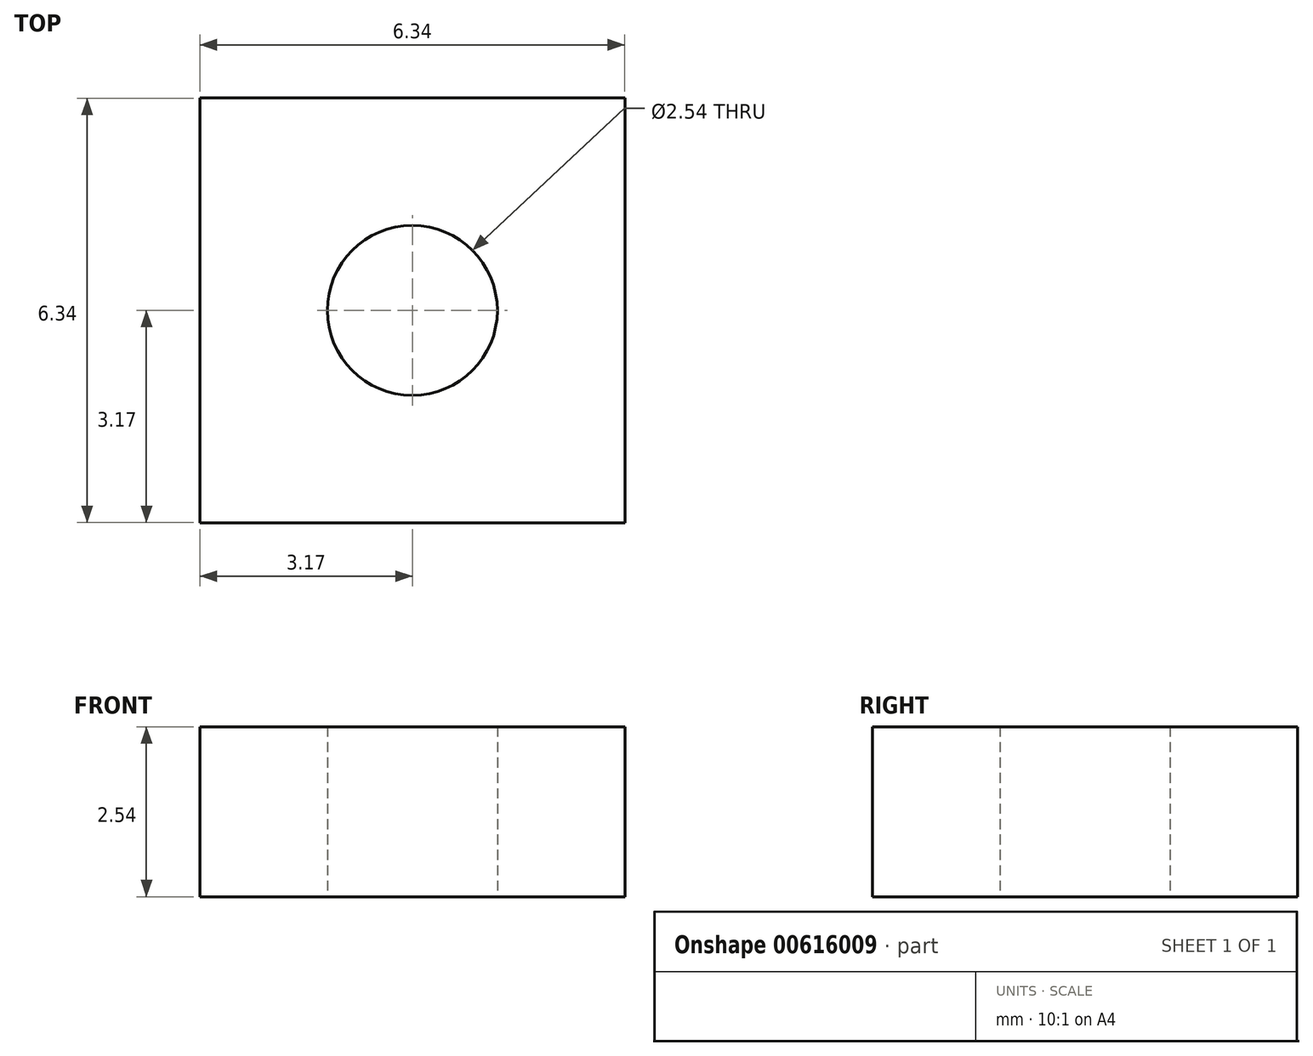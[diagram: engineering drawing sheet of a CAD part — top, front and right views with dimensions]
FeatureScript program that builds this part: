
annotation { "Feature Type Name" : "Feature", "Feature Type Description" : "" }
export const myFeature = defineFeature(function(context is Context, id is Id, definition is map)
    precondition{}
    {
        {
            var Q0;
            Q0=qCreatedBy(makeId("Top.planeOp"),FACE);
            var sketch = newSketch(context, id + "F0", { "sketchPlane" : qUnion([Q0])});
            skLineSegment(sketch, "E0.bottom", {"start": v(-3.18, 3.18) * mm, "end": v(3.17, 3.18) * mm});
            skLineSegment(sketch, "E0.top", {"start": v(-3.18, -3.18) * mm, "end": v(3.18, -3.18) * mm});
            skLineSegment(sketch, "E0.left", {"start": v(-3.18, 3.18) * mm, "end": v(-3.18, -3.18) * mm});
            skLineSegment(sketch, "E0.right", {"start": v(3.17, 3.18) * mm, "end": v(3.18, -3.18) * mm});
            skCircle(sketch, "E1", {"center": v(0, 0) * mm, "radius": 1.27 * mm});
            skSolve(sketch);
        }
        {
            var Q0;
            Q0 = qSketchRegion(id + "F0", true);
            extrude(context, id + "F1", {"entities" : qUnion([Q0]), "depth" : 2.54 * mm, "offsetDistance" : 25.4 * mm});
        }
    });
